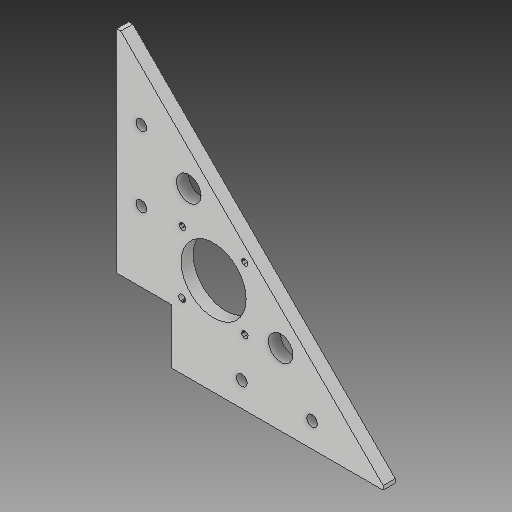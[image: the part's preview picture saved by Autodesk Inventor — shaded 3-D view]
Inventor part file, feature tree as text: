
AUTODESK INVENTOR PART (.ipt)
format: ipt  version: 2018 (Build 220112000, 112)  size: 424,448 bytes
history: native  units: mm
features: extrude x2, sketch x2
ambient origin geometry x8: Origin, YZ Plane, XZ Plane, XY Plane, X Axis, Y Axis, Z Axis, Center Point
bodies: Solid1 (feature_tree)
feature tree (4):
  extrude  "Extrusion1"  Depth=6.0mm
  extrude  "Extrusion3"  Depth=6.0mm
  sketch  "Sketch1"  dims[d0=6.0mm d1=0.0mm d2=5.3mm]
  sketch  "Sketch2"  dims[d3=5.3mm d4=5.3mm d5=5.3mm d6=3.2mm d7=3.2mm d8=3.2mm d9=3.2mm d10=12.2mm d11=12.2mm d12=32.2mm d15=6.0mm d16=0.0mm]
